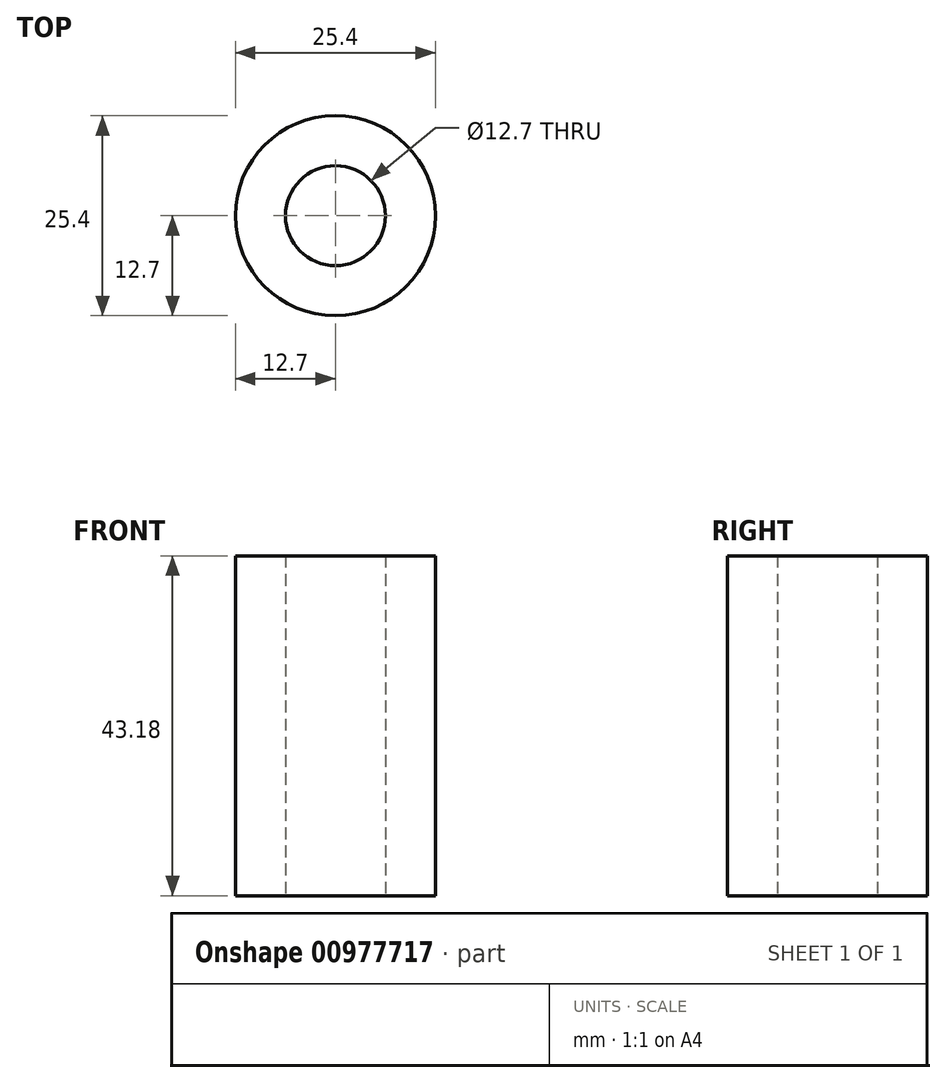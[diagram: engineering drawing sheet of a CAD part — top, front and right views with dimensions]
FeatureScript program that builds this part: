
annotation { "Feature Type Name" : "Feature", "Feature Type Description" : "" }
export const myFeature = defineFeature(function(context is Context, id is Id, definition is map)
    precondition{}
    {
        {
            var Q0;
            Q0=qCreatedBy(makeId("Top.planeOp"),FACE);
            var sketch = newSketch(context, id + "F0", { "sketchPlane" : qUnion([Q0])});
            skCircle(sketch, "E0", {"center": v(0, 0) * mm, "radius": 12.7 * mm});
            skCircle(sketch, "E1.0", {"center": v(0, 0) * mm, "radius": 6.35 * mm});
            skSolve(sketch);
        }
        {
            var Q0;
            Q0=makeQuery(id+"F0.imprint","IMPRINT",FACE,{"disambiguationData":[TD([[makeQuery(id+"F0.imprint","IMPRINT",EDGE,{"derivedFrom":sQuery(id+"F0.wireOp",EDGE,"E0")}),1.0]])]});
            extrude(context, id + "F1", {"entities" : qUnion([Q0]), "depth" : 43.18 * mm, "offsetDistance" : 25.4 * mm});
        }
    });
